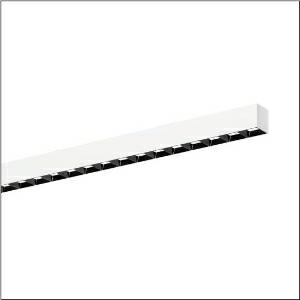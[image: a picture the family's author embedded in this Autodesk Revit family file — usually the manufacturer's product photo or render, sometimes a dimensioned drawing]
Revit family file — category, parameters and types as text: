
# Revit family: silica_r__21_51mx24tctaw_1b94
name_source: partatom
category: Lighting Fixtures
units: mm (PartAtom-declared; Revit-internal decimal feet)

## family parameters
Cut with Voids When Loaded = No
Host = Face
Light Source = No
Part Type = Normal
Room Calculation Point = No
Round Connector Dimension = Use Diameter
Shared = No

## types (1)
- --- (1 x LED, 8200 lm, 81.1 W, 6500K)
    Apparent Load = 81 VA
    CIE Flux Codes = 74 94 99 100 100
    Color Rendering = 80
    Color Temperature = 6500K
    Default Elevation = 1800 mm
    Description = Silica® 21, office luminaire, primary light control with darklight reflector, of PMMA, black, light emission: direct distribution, primary light characteristic: asymmetric, installation type: surface-mounted, LED, rated luminous flux: 8.200lm, luminous efficacy: 96lm/W, light colour: 8tw, colour temperature: 2700..6500K, control gear: DALI DT8, with terminal, 3+2-pole, max. 2.5mm², mains connection: 220..240V, AC, 50/60Hz, rated input power: 85.2W, luminaire housing, of aluminium, traffic white (RAL 9016), length: 3.004mm, width: 53mm, height: 53mm, protection rating (complete): IP20, insulation class (complete): insulation class I (protective earthing), certification: CE, permissible operating ambient temperature: 0..+35°C, standard: EN 50419, packaging unit: 1 piece
    Height = 53 mm
    Lamp = 1 x LED
    Lamp Light Flux = 8200 lm
    Lamp Power = 81.1 W
    Lamp count = 1
    Length = 3004 mm
    Luminous efficacy = 101 lm/W
    Manufacturer = Siteco
    ModVariant = No
    Model = 51MX24TCTAW
    Mounting Place = Ceiling
    Mounting Type = Surface mounted
    Number of Poles = 1
    OnlyDefault = Yes
    Power Factor = 1
    Product Name = Silica® 21
    Product group = office luminaire | ceiling mounted
    ProductGroupID = 302
    Protection Class = Protection class I
    Protection Degree = IP 20
    RLX_Detail_Level = 1
    RLX_Emergency_Light_Flux = 0 lm
    RLX_Emergency_Type = 0
    RLX_Emergency_Type_DB = No
    RlxData = <blob elided: 58801 chars, md5=cf62ce60>
    Socket = socket
    Standby Power = 0 W
    System Light Flux = 8200 lm
    System Power = 81 W
    Type Comments = individual setting
    Type Image = l_1335873.jpg
    URL = http://relux.com
    VarID = @adj_140004
    Voltage = 0 V
    Weight = 0.00 kg
    Width = 53 mm

## geometry (parser evidence)
native form markers: Blend x4, Sweep x11
no freeform markers — native parametric forms only
